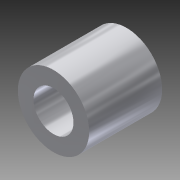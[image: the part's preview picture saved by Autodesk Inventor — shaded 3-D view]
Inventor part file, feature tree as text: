
AUTODESK INVENTOR PART (.ipt)
format: ipt  version: 2015 (Build 190159000, 159)  size: 88,576 bytes
history: native  units: in
note: dims shown in document units (in); Inventor stores cm internally (conversion verified against a paired STEP export)
features: extrude x1, sketch x1
ambient origin geometry x8: Origin, YZ Plane, XZ Plane, XY Plane, X Axis, Y Axis, Z Axis, Center Point
bodies: Solid1 (feature_tree)
feature tree (2):
  extrude  "Extrusion1"  Depth=0.256in
  sketch  "Sketch1"  dims[d0=0.14in d1=0.25in d2=0.256in d3=0.0in]
